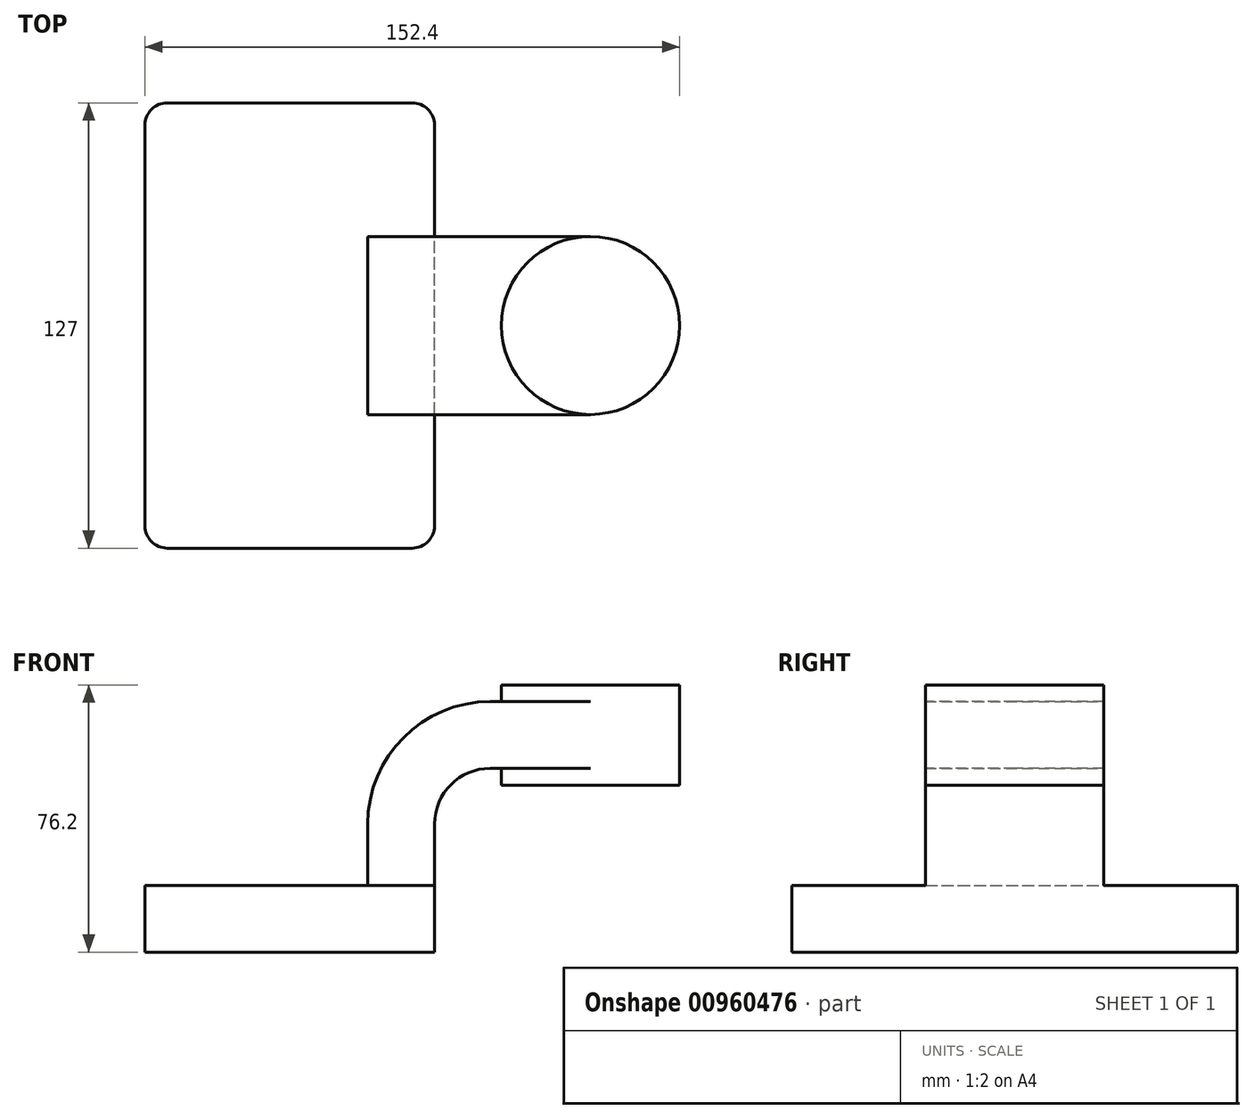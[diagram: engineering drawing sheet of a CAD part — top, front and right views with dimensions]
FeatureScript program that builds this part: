
annotation { "Feature Type Name" : "Feature", "Feature Type Description" : "" }
export const myFeature = defineFeature(function(context is Context, id is Id, definition is map)
    precondition{}
    {
        {
            var Q0;
            Q0=qCreatedBy(makeId("Front.planeOp"),FACE);
            var sketch = newSketch(context, id + "F0", { "sketchPlane" : qUnion([Q0])});
            skLineSegment(sketch, "E0.bottom", {"start": v(-42.83, 9.6) * mm, "end": v(39.72, 9.6) * mm});
            skLineSegment(sketch, "E0.top", {"start": v(-42.83, -9.46) * mm, "end": v(39.72, -9.46) * mm});
            skLineSegment(sketch, "E0.left", {"start": v(-42.83, 9.6) * mm, "end": v(-42.83, -9.46) * mm});
            skLineSegment(sketch, "E0.right", {"start": v(39.72, 9.6) * mm, "end": v(39.72, -9.46) * mm});
            skLineSegment(sketch, "E1.bottom", {"start": v(58.77, 66.74) * mm, "end": v(109.57, 66.74) * mm});
            skLineSegment(sketch, "E1.top", {"start": v(58.77, 38.17) * mm, "end": v(109.57, 38.17) * mm});
            skLineSegment(sketch, "E1.left", {"start": v(58.77, 66.74) * mm, "end": v(58.77, 38.17) * mm});
            skLineSegment(sketch, "E1.right", {"start": v(109.57, 66.74) * mm, "end": v(109.57, 38.17) * mm});
            skPoint(sketch, "E1.middle", {"position": v(84.17, 52.46) * mm});
            skLineSegment(sketch, "E2", {"start": v(39.72, 9.6) * mm, "end": v(39.72, 27.07) * mm});
            skArc(sketch, "E3", {"start": v(39.72, 27.07) * mm, "mid": v(44.37, 38.3) * mm, "end": v(55.6, 42.94) * mm});
            skLineSegment(sketch, "E4", {"start": v(55.6, 42.94) * mm, "end": v(84.17, 42.94) * mm});
            skLineSegment(sketch, "E5.0", {"start": v(55.6, 62) * mm, "end": v(84.17, 62) * mm});
            skArc(sketch, "E5.1", {"start": v(20.67, 27.07) * mm, "mid": v(30.9, 51.76) * mm, "end": v(55.6, 62) * mm});
            skLineSegment(sketch, "E5.2", {"start": v(20.67, 6.1) * mm, "end": v(20.67, 27.07) * mm});
            skLineSegment(sketch, "E6", {"start": v(84.17, 38.17) * mm, "end": v(84.17, 66.74) * mm});
            skFitSpline(sketch, "E7", {"points": [v(-42.83, 9.6) * mm, v(55.6, 62) * mm], "startDerivative": vector(-0.8, 92.6) * mm, "endDerivative": vector(131.44, -0.77) * mm});
            skSolve(sketch);
        }
        {
            var Q0;
            Q0=makeQuery(id+"F0.imprint","IMPRINT",FACE,{"disambiguationData":[TD([[makeQuery(id+"F0.imprint","IMPRINT",EDGE,{"derivedFrom":sQuery(id+"F0.wireOp",EDGE,"E0.top")}),1.0]])]});
            extrude(context, id + "F1", {"entities" : qUnion([Q0]), "endBound" : BoundingType.SYMMETRIC, "depth" : 127 * mm, "offsetDistance" : 25.4 * mm});
        }
        {
            var Q0;
            {var subQ1=sQuery(id+"F0.wireOp",EDGE,"E2");Q0=makeQuery(id+"F0.imprint","IMPRINT",FACE,{"disambiguationData":[TD([[makeQuery(id+"F0.imprint","IMPRINT",EDGE,{"derivedFrom":subQ1}),1.0]])]});}
            var Q1;
            {var subQ0=sQuery(id+"F0.wireOp",EDGE,"E5.0");var subQ1=sQuery(id+"F0.wireOp",EDGE,"E1.left");var subQ2=makeQuery(id+"F0.imprint","INTERSECT",VERTEX,{"derivedFrom":[subQ1,subQ0]});Q1=makeQuery(id+"F0.imprint","IMPRINT",FACE,{"disambiguationData":[TD([[makeQuery(id+"F0.imprint","IMPRINT",EDGE,{"disambiguationData":[TD([[subQ2,-1.0]])],"derivedFrom":subQ1}),1.0]])]});}
            extrude(context, id + "F2", {"entities" : qUnion([Q0, Q1]), "operationType" : NewBodyOperationType.ADD, "endBound" : BoundingType.SYMMETRIC, "depth" : 50.8 * mm, "offsetDistance" : 25.4 * mm});
        }
        {
            var Q0;
            {var subQ4=sQuery(id+"F0.wireOp",EDGE,"E5.1");Q0=makeQuery(id+"F0.imprint","IMPRINT",FACE,{"disambiguationData":[TD([[makeQuery(id+"F0.imprint","IMPRINT",EDGE,{"derivedFrom":subQ4}),1.0]])]});}
            extrude(context, id + "F3", {"entities" : qUnion([Q0]), "operationType" : NewBodyOperationType.ADD, "endBound" : BoundingType.SYMMETRIC, "depth" : 15.88 * mm, "offsetDistance" : 25.4 * mm});
        }
        {
            var Q0;
            {var subQ0=sQuery(id+"F0.wireOp",EDGE,"E1.right");Q0=makeQuery(id+"F0.imprint","IMPRINT",FACE,{"disambiguationData":[TD([[makeQuery(id+"F0.imprint","IMPRINT",EDGE,{"derivedFrom":subQ0}),-1.0]])]});}
            var Q1;
            Q1=sQuery(id+"F0.wireOp",EDGE,"E6");
            revolve(context, id + "F4", {"operationType" : NewBodyOperationType.ADD, "surfaceOperationType" : NewSurfaceOperationType.NEW, "entities" : qUnion([Q0]), "axis" : qUnion([Q1]), "revolveType" : RevolveType.FULL});
        }
        {
            var Q0;
            Q0=makeQuery(id+"F1.opExtrude","CAP_EDGE",EDGE,{"disambiguationData":[OSD([sQuery(id+"F0.wireOp",EDGE,"E0.left")])],"isStart":false});
            var Q1;
            Q1=makeQuery(id+"F1.opExtrude","CAP_EDGE",EDGE,{"disambiguationData":[OSD([sQuery(id+"F0.wireOp",EDGE,"E0.right")])],"isStart":false});
            var Q2;
            Q2=makeQuery(id+"F1.opExtrude","CAP_EDGE",EDGE,{"disambiguationData":[OSD([sQuery(id+"F0.wireOp",EDGE,"E0.right")])],"isStart":true});
            var Q3;
            Q3=makeQuery(id+"F1.opExtrude","CAP_EDGE",EDGE,{"disambiguationData":[OSD([sQuery(id+"F0.wireOp",EDGE,"E0.left")])],"isStart":true});
            fillet(context, id + "F5", {"entities" : qUnion([Q0, Q1, Q2, Q3]), "radius" : 6.35 * mm, "tangentPropagation" : true, "allowEdgeOverflow" : false});
        }
    });
